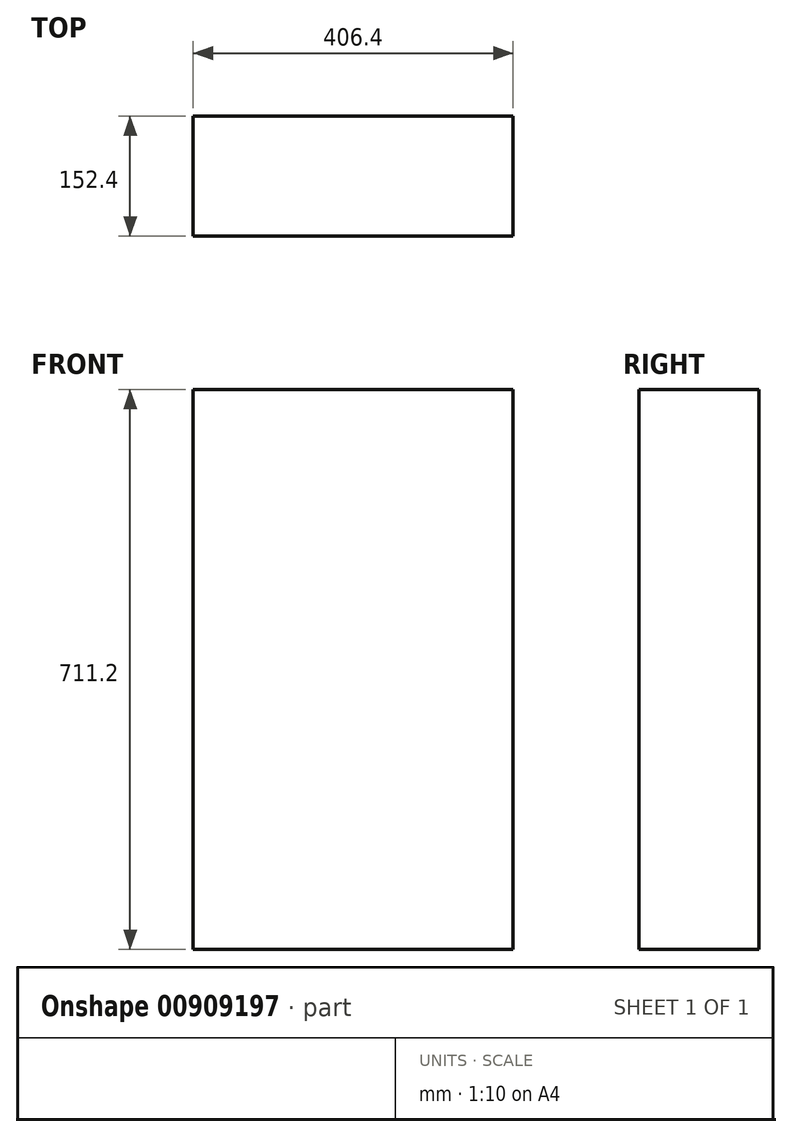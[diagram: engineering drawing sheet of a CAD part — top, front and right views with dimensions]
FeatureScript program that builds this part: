
annotation { "Feature Type Name" : "Feature", "Feature Type Description" : "" }
export const myFeature = defineFeature(function(context is Context, id is Id, definition is map)
    precondition{}
    {
        {
            var Q0;
            Q0=qCreatedBy(makeId("Front.planeOp"),FACE);
            var sketch = newSketch(context, id + "F0", { "sketchPlane" : qUnion([Q0])});
            skLineSegment(sketch, "E0.bottom", {"start": v(-189.88, 404.62) * mm, "end": v(216.52, 404.62) * mm});
            skLineSegment(sketch, "E0.top", {"start": v(-189.88, -306.58) * mm, "end": v(216.52, -306.58) * mm});
            skLineSegment(sketch, "E0.left", {"start": v(-189.88, 404.62) * mm, "end": v(-189.88, -306.58) * mm});
            skLineSegment(sketch, "E0.right", {"start": v(216.52, 404.62) * mm, "end": v(216.52, -306.58) * mm});
            skSolve(sketch);
        }
        {
            var Q0;
            Q0=makeQuery(id+"F0.imprint","IMPRINT",FACE,{"disambiguationData":[TD([[makeQuery(id+"F0.imprint","IMPRINT",EDGE,{"derivedFrom":sQuery(id+"F0.wireOp",EDGE,"E0.bottom")}),-1.0]])]});
            extrude(context, id + "F1", {"entities" : qUnion([Q0]), "depth" : 152.4 * mm, "offsetDistance" : 25.4 * mm});
        }
    });
